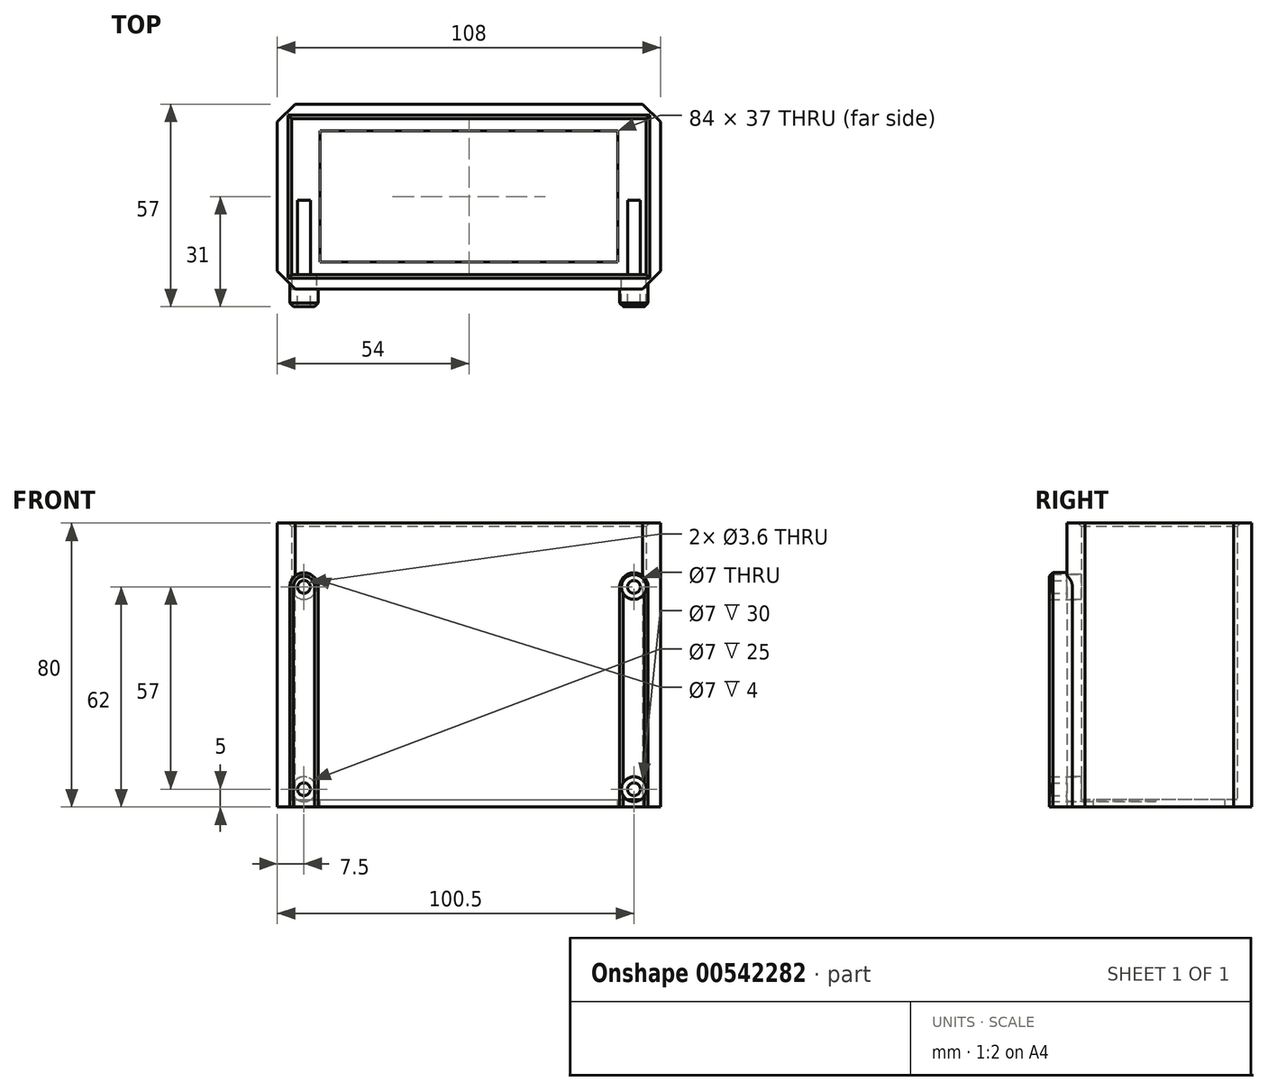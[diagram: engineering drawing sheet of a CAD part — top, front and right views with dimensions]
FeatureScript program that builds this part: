
annotation { "Feature Type Name" : "Feature", "Feature Type Description" : "" }
export const myFeature = defineFeature(function(context is Context, id is Id, definition is map)
    precondition{}
    {
        {
            var Q0;
            Q0=qCreatedBy(makeId("Top.planeOp"),FACE);
            var sketch = newSketch(context, id + "F0", { "sketchPlane" : qUnion([Q0])});
            skLineSegment(sketch, "E0.bottom", {"start": v(-50, 22) * mm, "end": v(50, 22) * mm});
            skLineSegment(sketch, "E0.top", {"start": v(-50, -22) * mm, "end": v(50, -22) * mm});
            skLineSegment(sketch, "E0.left", {"start": v(-50, 22) * mm, "end": v(-50, -22) * mm});
            skLineSegment(sketch, "E0.right", {"start": v(50, 22) * mm, "end": v(50, -22) * mm});
            skPoint(sketch, "E0.middle", {"position": v(0, 0) * mm});
            skLineSegment(sketch, "E1.0", {"start": v(-54, 26) * mm, "end": v(54, 26) * mm});
            skLineSegment(sketch, "E1.1", {"start": v(-54, 26) * mm, "end": v(-54, -26) * mm});
            skLineSegment(sketch, "E1.2", {"start": v(-54, -26) * mm, "end": v(54, -26) * mm});
            skLineSegment(sketch, "E1.3", {"start": v(54, 26) * mm, "end": v(54, -26) * mm});
            skSolve(sketch);
        }
        {
            var Q0;
            Q0=makeQuery(id+"F0.imprint","IMPRINT",FACE,{"disambiguationData":[TD([[makeQuery(id+"F0.imprint","IMPRINT",EDGE,{"derivedFrom":sQuery(id+"F0.wireOp",EDGE,"E0.bottom")}),1.0]])]});
            extrude(context, id + "F1", {"entities" : qUnion([Q0]), "depth" : 80 * mm, "offsetDistance" : 25 * mm});
        }
        {
            var Q0;
            Q0=makeQuery(id+"F0.imprint","IMPRINT",FACE,{"disambiguationData":[TD([[makeQuery(id+"F0.imprint","IMPRINT",EDGE,{"derivedFrom":sQuery(id+"F0.wireOp",EDGE,"E0.bottom")}),-1.0]])]});
            extrude(context, id + "F2", {"entities" : qUnion([Q0]), "operationType" : NewBodyOperationType.ADD, "depth" : 2 * mm, "offsetDistance" : 25 * mm});
        }
        {
            var Q0;
            Q0=makeQuery(id+"F1.opExtrude","SWEPT_FACE",FACE,{"disambiguationData":[OSD([sQuery(id+"F0.wireOp",EDGE,"E1.2")])]});
            var sketch = newSketch(context, id + "F3", { "sketchPlane" : qUnion([Q0])});
            skLineSegment(sketch, "E2.bottom", {"start": v(-46.5, 62) * mm, "end": v(46.5, 62) * mm, "construction": true});
            skLineSegment(sketch, "E2.top", {"start": v(-46.5, 5) * mm, "end": v(46.5, 5) * mm, "construction": true});
            skLineSegment(sketch, "E2.left", {"start": v(-46.5, 62) * mm, "end": v(-46.5, 5) * mm, "construction": true});
            skLineSegment(sketch, "E2.right", {"start": v(46.5, 62) * mm, "end": v(46.5, 5) * mm, "construction": true});
            skArc(sketch, "E3", {"start": v(-42.5, 62) * mm, "mid": v(-46.5, 66) * mm, "end": v(-50.5, 62) * mm});
            skLineSegment(sketch, "E4", {"start": v(-50.5, 62) * mm, "end": v(-50.5, 0) * mm});
            skLineSegment(sketch, "E5", {"start": v(-42.5, 62) * mm, "end": v(-42.5, 0) * mm});
            skCircle(sketch, "E6", {"center": v(-46.5, 62) * mm, "radius": 1.8 * mm});
            skCircle(sketch, "E7", {"center": v(-46.5, 5) * mm, "radius": 1.8 * mm});
            skLineSegment(sketch, "E8", {"start": v(0, 0) * mm, "end": v(0, 80) * mm, "construction": true});
            skCircle(sketch, "E9.MirrorC", {"center": v(46.5, 62) * mm, "radius": 1.8 * mm});
            skLineSegment(sketch, "E10.MirrorCS", {"start": v(42.5, 62) * mm, "end": v(42.5, 0) * mm});
            skArc(sketch, "E11.MirrorCS", {"start": v(42.5, 62) * mm, "mid": v(46.5, 66) * mm, "end": v(50.5, 62) * mm});
            skLineSegment(sketch, "E12.MirrorCS", {"start": v(50.5, 62) * mm, "end": v(50.5, 0) * mm});
            skCircle(sketch, "E13.MirrorC", {"center": v(46.5, 5) * mm, "radius": 1.8 * mm});
            skCircle(sketch, "E14", {"center": v(-46.5, 62) * mm, "radius": 3.5 * mm});
            skCircle(sketch, "E15", {"center": v(-46.5, 5) * mm, "radius": 3.5 * mm});
            skCircle(sketch, "E16.MirrorC", {"center": v(46.5, 62) * mm, "radius": 3.5 * mm});
            skCircle(sketch, "E17.MirrorC", {"center": v(46.5, 5) * mm, "radius": 3.5 * mm});
            skSolve(sketch);
        }
        {
            var Q0;
            Q0=makeQuery(id+"F3.imprint","IMPRINT",FACE,{"disambiguationData":[TD([[makeQuery(id+"F3.imprint","IMPRINT",EDGE,{"derivedFrom":sQuery(id+"F3.wireOp",EDGE,"E9.MirrorC")}),1.0]])]});
            var Q1;
            Q1=makeQuery(id+"F3.imprint","IMPRINT",FACE,{"disambiguationData":[TD([[makeQuery(id+"F3.imprint","IMPRINT",EDGE,{"derivedFrom":sQuery(id+"F3.wireOp",EDGE,"E3")}),1.0]])]});
            var Q2;
            Q2=makeQuery(id+"F3.imprint","IMPRINT",FACE,{"disambiguationData":[TD([[makeQuery(id+"F3.imprint","IMPRINT",EDGE,{"derivedFrom":sQuery(id+"F3.wireOp",EDGE,"E6")}),-1.0]])]});
            var Q3;
            Q3=makeQuery(id+"F3.imprint","IMPRINT",FACE,{"disambiguationData":[TD([[makeQuery(id+"F3.imprint","IMPRINT",EDGE,{"derivedFrom":sQuery(id+"F3.wireOp",EDGE,"E7")}),-1.0]])]});
            var Q4;
            {var subQ1=sQuery(id+"F3.wireOp",EDGE,"E10.MirrorCS");Q4=makeQuery(id+"F3.imprint","IMPRINT",FACE,{"disambiguationData":[TD([[makeQuery(id+"F3.imprint","IMPRINT",EDGE,{"derivedFrom":subQ1}),1.0]])]});}
            var Q5;
            Q5=makeQuery(id+"F3.imprint","IMPRINT",FACE,{"disambiguationData":[TD([[makeQuery(id+"F3.imprint","IMPRINT",EDGE,{"derivedFrom":sQuery(id+"F3.wireOp",EDGE,"E13.MirrorC")}),1.0]])]});
            extrude(context, id + "F4", {"entities" : qUnion([Q0, Q1, Q2, Q3, Q4, Q5]), "operationType" : NewBodyOperationType.ADD, "depth" : 5 * mm, "offsetDistance" : 25 * mm});
        }
        {
            var Q0;
            Q0=makeQuery(id+"F3.imprint","IMPRINT",FACE,{"disambiguationData":[TD([[makeQuery(id+"F3.imprint","IMPRINT",EDGE,{"derivedFrom":sQuery(id+"F3.wireOp",EDGE,"E7")}),-1.0]])]});
            var Q1;
            Q1=makeQuery(id+"F3.imprint","IMPRINT",FACE,{"disambiguationData":[TD([[makeQuery(id+"F3.imprint","IMPRINT",EDGE,{"derivedFrom":sQuery(id+"F3.wireOp",EDGE,"E13.MirrorC")}),1.0]])]});
            var Q2;
            Q2=makeQuery(id+"F3.imprint","IMPRINT",FACE,{"disambiguationData":[TD([[makeQuery(id+"F3.imprint","IMPRINT",EDGE,{"derivedFrom":sQuery(id+"F3.wireOp",EDGE,"E9.MirrorC")}),1.0]])]});
            var Q3;
            Q3=makeQuery(id+"F3.imprint","IMPRINT",FACE,{"disambiguationData":[TD([[makeQuery(id+"F3.imprint","IMPRINT",EDGE,{"derivedFrom":sQuery(id+"F3.wireOp",EDGE,"E9.MirrorC")}),-1.0]])]});
            var Q4;
            Q4=makeQuery(id+"F3.imprint","IMPRINT",FACE,{"disambiguationData":[TD([[makeQuery(id+"F3.imprint","IMPRINT",EDGE,{"derivedFrom":sQuery(id+"F3.wireOp",EDGE,"E13.MirrorC")}),-1.0]])]});
            var Q5;
            Q5=makeQuery(id+"F3.imprint","IMPRINT",FACE,{"disambiguationData":[TD([[makeQuery(id+"F3.imprint","IMPRINT",EDGE,{"derivedFrom":sQuery(id+"F3.wireOp",EDGE,"E7")}),1.0]])]});
            var Q6;
            Q6=makeQuery(id+"F3.imprint","IMPRINT",FACE,{"disambiguationData":[TD([[makeQuery(id+"F3.imprint","IMPRINT",EDGE,{"derivedFrom":sQuery(id+"F3.wireOp",EDGE,"E6")}),-1.0]])]});
            var Q7;
            Q7=makeQuery(id+"F3.imprint","IMPRINT",FACE,{"disambiguationData":[TD([[makeQuery(id+"F3.imprint","IMPRINT",EDGE,{"derivedFrom":sQuery(id+"F3.wireOp",EDGE,"E6")}),1.0]])]});
            extrude(context, id + "F5", {"entities" : qUnion([Q0, Q1, Q2, Q3, Q4, Q5, Q6, Q7]), "operationType" : NewBodyOperationType.REMOVE, "oppositeDirection" : true, "depth" : 25 * mm, "offsetDistance" : 25 * mm});
        }
        {
            var Q0;
            Q0=makeQuery(id+"F1.opExtrude","SWEPT_EDGE",EDGE,{"disambiguationData":[OSD([sQuery(id+"F0.wireOp",EDGE,"E1.0"),sQuery(id+"F0.wireOp",EDGE,"E1.3")])]});
            var Q1;
            Q1=makeQuery(id+"F1.opExtrude","SWEPT_EDGE",EDGE,{"disambiguationData":[OSD([sQuery(id+"F0.wireOp",EDGE,"E1.2"),sQuery(id+"F0.wireOp",EDGE,"E1.3")])]});
            var Q2;
            Q2=makeQuery(id+"F1.opExtrude","SWEPT_EDGE",EDGE,{"disambiguationData":[OSD([sQuery(id+"F0.wireOp",EDGE,"E1.1"),sQuery(id+"F0.wireOp",EDGE,"E1.2")])]});
            var Q3;
            Q3=makeQuery(id+"F1.opExtrude","SWEPT_EDGE",EDGE,{"disambiguationData":[OSD([sQuery(id+"F0.wireOp",EDGE,"E1.0"),sQuery(id+"F0.wireOp",EDGE,"E1.1")])]});
            chamfer(context, id + "F6", {"entities" : qUnion([Q0, Q1, Q2, Q3]), "width" : 5 * mm, "tangentPropagation" : true});
        }
        {
            var Q0;
            Q0=makeQuery(id+"F1.opExtrude","CAP_EDGE",EDGE,{"disambiguationData":[OSD([sQuery(id+"F0.wireOp",EDGE,"E0.bottom")])],"isStart":false});
            var Q1;
            Q1=makeQuery(id+"F1.opExtrude","CAP_EDGE",EDGE,{"disambiguationData":[OSD([sQuery(id+"F0.wireOp",EDGE,"E0.left")])],"isStart":false});
            var Q2;
            Q2=makeQuery(id+"F1.opExtrude","CAP_EDGE",EDGE,{"disambiguationData":[OSD([sQuery(id+"F0.wireOp",EDGE,"E0.top")])],"isStart":false});
            var Q3;
            Q3=makeQuery(id+"F1.opExtrude","CAP_EDGE",EDGE,{"disambiguationData":[OSD([sQuery(id+"F0.wireOp",EDGE,"E0.right")])],"isStart":false});
            var Q4;
            Q4=makeQuery(id+"F4.opExtrude","CAP_EDGE",EDGE,{"disambiguationData":[OSD([sQuery(id+"F3.wireOp",EDGE,"E5")])],"isStart":false});
            var Q5;
            Q5=makeQuery(id+"F4.opExtrude","CAP_EDGE",EDGE,{"disambiguationData":[OSD([sQuery(id+"F3.wireOp",EDGE,"E4")])],"isStart":false});
            var Q6;
            Q6=makeQuery(id+"F4.opExtrude","CAP_EDGE",EDGE,{"disambiguationData":[OSD([sQuery(id+"F3.wireOp",EDGE,"E10.MirrorCS")])],"isStart":false});
            chamfer(context, id + "F7", {"entities" : qUnion([Q0, Q1, Q2, Q3, Q4, Q5, Q6]), "width" : 1 * mm, "tangentPropagation" : true});
        }
        {
            var Q0;
            Q0=makeQuery(id+"F2.opExtrude","CAP_FACE",FACE,{"disambiguationData":[OSD([sQuery(id+"F0.wireOp",EDGE,"E0.bottom"),sQuery(id+"F0.wireOp",EDGE,"E0.top"),sQuery(id+"F0.wireOp",EDGE,"E0.left"),sQuery(id+"F0.wireOp",EDGE,"E0.right")])],"isStart":false});
            var sketch = newSketch(context, id + "F8", { "sketchPlane" : qUnion([Q0])});
            skLineSegment(sketch, "E18.bottom", {"start": v(-42, 18.5) * mm, "end": v(42, 18.5) * mm});
            skLineSegment(sketch, "E18.top", {"start": v(-42, -18.5) * mm, "end": v(42, -18.5) * mm});
            skLineSegment(sketch, "E18.left", {"start": v(-42, 18.5) * mm, "end": v(-42, -18.5) * mm});
            skLineSegment(sketch, "E18.right", {"start": v(42, 18.5) * mm, "end": v(42, -18.5) * mm});
            skPoint(sketch, "E18.middle", {"position": v(0, 0) * mm});
            skSolve(sketch);
        }
        {
            var Q0;
            {var subQ1=sQuery(id+"F8.wireOp",EDGE,"E18.bottom");Q0=makeQuery(id+"F8.imprint","IMPRINT",FACE,{"disambiguationData":[TD([[makeQuery(id+"F8.imprint","IMPRINT",EDGE,{"derivedFrom":subQ1}),-1.0]])]});}
            extrude(context, id + "F9", {"entities" : qUnion([Q0]), "operationType" : NewBodyOperationType.REMOVE, "oppositeDirection" : true, "depth" : 25 * mm, "offsetDistance" : 25 * mm});
        }
    });
